# Revit family: Промежуточная секция - стандартная LITENED PS
name_source: partatom
category: Оборудование
revit_build: Autodesk Revit 2017 (Build: 20160225_1515(x64)
units: mm (PartAtom-declared; Revit-internal decimal feet)

## family parameters
Всегда вертикально = Да
На основе рабочей плоскости = Нет
Общий = Нет
При загрузке вырезать с полостями = Нет
Размер круглого соединителя = Использовать диаметр
Тип детали = Нормальный
Точка расчета площади = Нет

## types (8) — shared parameters
L = 350 мм
h = 60 мм
В1 = 275 мм
Д = 350 мм
Д1 = 330 мм
Единица измерения = шт.
Завод изготовитель = NED
Ключевая пометка = Вентиляция
Наименование и тех.хар-ка = Промежуточная секция - стандартная
Раздел = ОВ
высота ножек = 50 мм
zero-valued in all types: Г1, Мощность, кВт

## per-type parameters (varying)
| type | А | А1 | Б | Б1 | Г | Масса единицы | Материал | Тип, марка, обозначение | высота | размер В | ширина |
| PS 50-25 | 710 мм | 690 мм | 470 мм | 450 мм | 395 мм | 12,5 | RAL 0000 Серый металл | LITENED 50-25 PS | 250 мм | 635 мм | 500 мм |
| PS 50-30 | 710 мм | 690 мм | 520 мм | 500 мм | 445 мм | 13 | Сталь серая | LITENED 50-30 PS | 300 мм | 635 мм | 500 мм |
| PS 60-30 | 810 мм | 790 мм | 520 мм | 500 мм | 445 мм | 14 | Сталь серая | LITENED 60-30 PS | 300 мм | 735 мм | 600 мм |
| PS 60-35 | 810 мм | 790 мм | 570 мм | 550 мм | 495 мм | 14.2 | Сталь серая | LITENED 60-35 PS | 350 мм | 735 мм | 600 мм |
| PS 70-40 | 910 мм | 890 мм | 620 мм | 600 мм | 545 мм | 15.5 | Сталь серая | LITENED 70-40 PS | 400 мм | 835 мм | 700 мм |
| PS 80-50 | 1010 мм | 990 мм | 720 мм | 700 мм | 645 мм | 17.5 | Сталь серая | LITENED 80-50 PS | 500 мм | 935 мм | 800 мм |
| PS 90-50 | 1125 мм | 1105 мм | 740 мм | 720 мм | 645 мм | 47.5 | Сталь серая | LITENED 90-50 PS | 500 мм | 1050 мм | 900 мм |
| PS 100-50 | 1225 мм | 1205 мм | 740 мм | 720 мм | 665 мм | 19.5 | Сталь серая | LITENED 100-50 PS | 500 мм | 1150 мм | 1000 мм |
